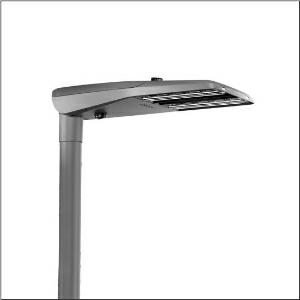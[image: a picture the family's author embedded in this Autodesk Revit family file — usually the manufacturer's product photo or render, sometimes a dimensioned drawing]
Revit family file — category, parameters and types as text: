
# Revit family: streetlight_sl_11_iq_midi___st1_0p1_0_5xc3k51y08me_73ea
name_source: partatom
category: Lighting Fixtures
units: mm (PartAtom-declared; Revit-internal decimal feet)

## family parameters
Cut with Voids When Loaded = No
Host = Face
Light Source = No
Part Type = Normal
Room Calculation Point = No
Round Connector Dimension = Use Diameter
Shared = No

## types (1)
- --- (1 x LED, 17540 lm, 122.7 W, 3000K)
    Apparent Load = 123 VA
    CIE Flux Codes = 32 65 95 100 100
    Color Rendering = 70
    Color Temperature = 3000K
    Default Elevation = 1800 mm
    Description = Streetlight SL 11 iQ midi, mast luminaire, primary light control with 3 zone facetted reflector, of plastic, silver coated, highly specular, primary optical cover: cover, of PMMA, transparent, light distribution: ST1.0P1.0, light emission: direct distribution, primary light characteristic: asymmetric, installation type: post-top, side-entry, lamps: LED, High Power LED, rated values: 17.540lm | 122,7W | 143lm/W (begin service life); end service life: 17.540lm | 130,2W; at 50% lumin. flux: 8.770lm | 56,1W | 156,3lm/W, colour temperature: 3000K, colour rendering: CRI > 70, light colour: 730, light setting 1 begin service life: 100% | 17.540lm | 122,7W | 143lm/W | 3.000K, light setting 1 end service life: 130,2W, further light settings possible, control: pre-setting: logarithmic dimming characteristic, Street-Remote, Auto-Match, Temp-Guard, Lumen-Switch, Night-Set, Smart-Wire, Light-Fading, Desk-Remote (wireless, voltage-free reading and setting of iQ features in the workshop via application-optimized NFC function/RFID function), optimised constant luminous flux control (CLO 2.0), with cable H07RN-F 5x 1.5mm², mains connection: 230..240V, AC, 50/60Hz, connection cable pre-assembled, cable length: 12,5m, luminaire housing, of diecast aluminium, powder-coated, Siteco® metallic grey (DB 702S), please order mast flange separately, inclination adjustable without tools: 0°, 5°, 10°, 15° (post-top) | 0°, -5°, -10°, -15° (side-entry), sealing non-destructively replaceable, multi-level sealing system, length: 780mm, width: 376mm, height: 118mm, mast flange for spigot size: 42mm (side-entry): 5XC10008XM4, 60/48mm (side-entry/post-top): 5XC10108XM2, 76/60mm (side-entry/post-top): 5XC10108XM1, equipment: Power, Smart Interface below and above, protection rating (complete): IP66, insulation class (complete): insulation class II (safety insulation), certification: CE, ENEC, ENEC+, VDE, UKCA, impact resistance: IK10, permissible operating ambient temperature for outdoor applications: -25..+50°C, standard-compliant lighting for roads and squares, Environmental Product Declaration (EPD) tested and certified by an independent institute, packaging unit: 1 piece

Light Distribution: ST1.0P1.0
    Height = 118 mm
    Lamp = 1 x LED
    Lamp Light Flux = 17540 lm
    Lamp Power = 122.7 W
    Lamp count = 1
    Length = 780 mm
    Luminous efficacy = 143 lm/W
    Manufacturer = Siteco
    ModVariant = No
    Model = 5XC3K51Y08ME
    Number of Poles = 1
    OnlyDefault = Yes
    Power Factor = 1
    Product Name = Streetlight SL 11 iQ midi | ST1.0P1.0
    Product group = mast luminaire | pylon top
    ProductGroupID = 6100
    Protection Class = Protection class II
    Protection Degree = IP 66
    RLX_Detail_Level = 1
    RLX_Emergency_Light_Flux = 0 lm
    RLX_Emergency_Type = 0
    RLX_Emergency_Type_DB = No
    RlxData = <blob elided: 69877 chars, md5=ee22b20d>
    Socket = socket
    Standby Power = 0 W
    System Light Flux = 17540 lm
    System Power = 123 W
    Type Comments = factory setting: luminous flux: 100 % | dim-lin: 254 | 553 mA
    Type Image = l_1004429.jpg
    URL = http://relux.com
    VarID = @adj_061435
    Voltage = 0 V
    Weight = 0.00 kg
    Width = 376 mm

## geometry (parser evidence)
native form markers: Blend x4, Sweep x10
no freeform markers — native parametric forms only
